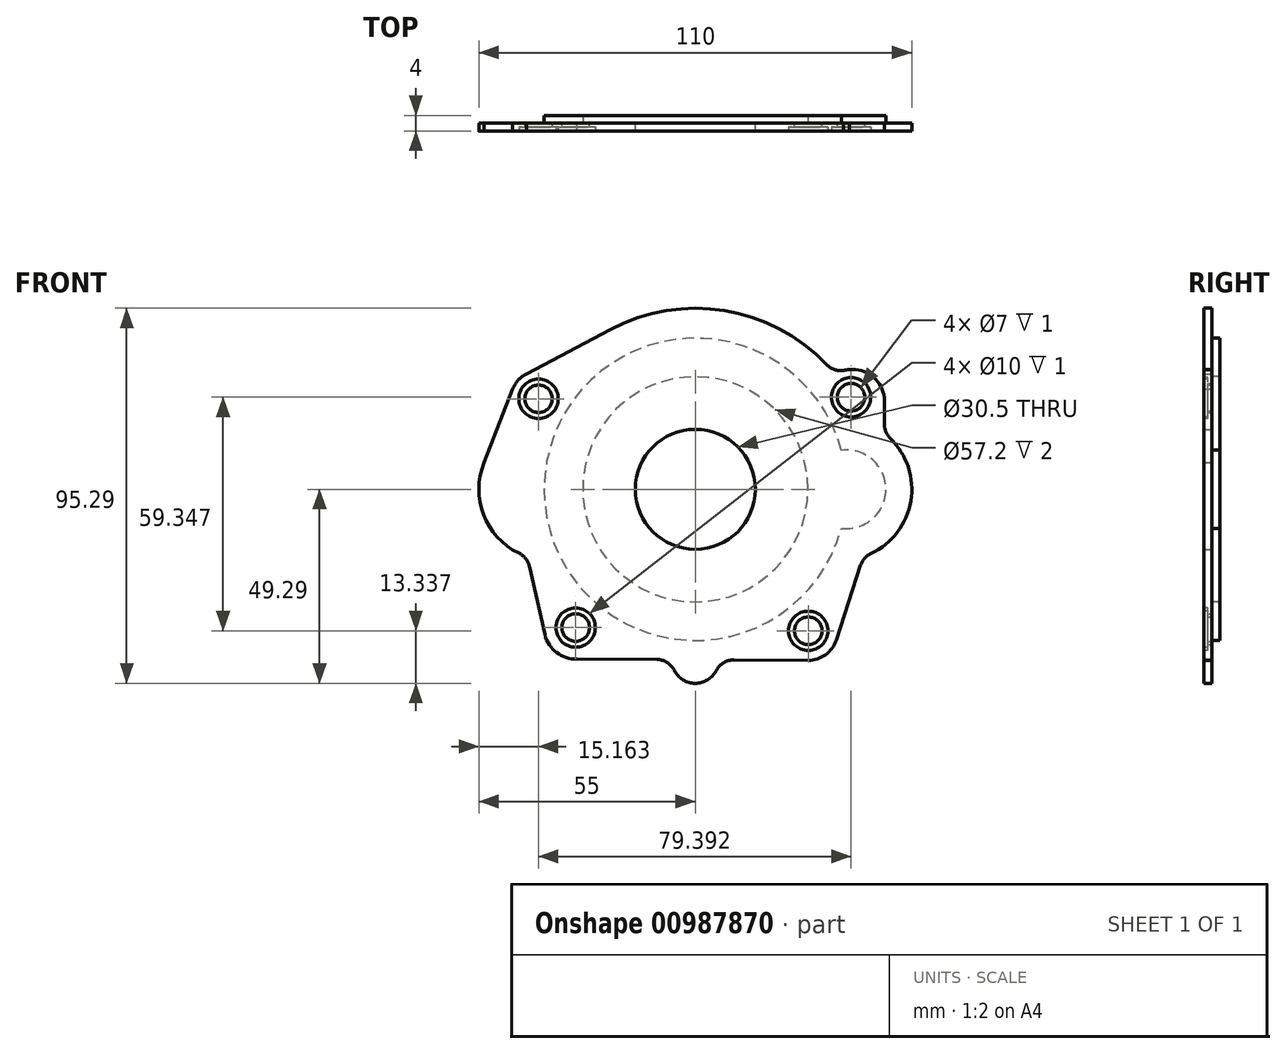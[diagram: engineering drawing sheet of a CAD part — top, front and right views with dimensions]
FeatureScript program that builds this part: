
annotation { "Feature Type Name" : "Feature", "Feature Type Description" : "" }
export const myFeature = defineFeature(function(context is Context, id is Id, definition is map)
    precondition{}
    {
        {
            var Q0;
            Q0=qCreatedBy(makeId("Front.planeOp"),FACE);
            var sketch = newSketch(context, id + "F0", { "sketchPlane" : qUnion([Q0])});
            skCircle(sketch, "E0", {"center": v(0, 0) * mm, "radius": 15.25 * mm});
            skCircle(sketch, "E1", {"center": v(-39.84, 23) * mm, "radius": 3.5 * mm});
            skCircle(sketch, "E2", {"center": v(-30.4, -35.12) * mm, "radius": 3.5 * mm});
            skCircle(sketch, "E3", {"center": v(28.7, -35.95) * mm, "radius": 3.5 * mm});
            skCircle(sketch, "E4", {"center": v(39.55, 23.4) * mm, "radius": 3.5 * mm});
            skArc(sketch, "E5", {"start": v(-42.72, -17.07) * mm, "mid": v(-39.64, -23.34) * mm, "end": v(-35.64, -29.08) * mm});
            skArc(sketch, "E6", {"start": v(-35.89, 28.78) * mm, "mid": v(-45.9, 26.5) * mm, "end": v(-42.87, 16.69) * mm});
            skArc(sketch, "E7", {"start": v(-35.64, -29.08) * mm, "mid": v(-35.64, -41.17) * mm, "end": v(-23.67, -39.44) * mm});
            skArc(sketch, "E8", {"start": v(22.47, -40.14) * mm, "mid": v(33.37, -41.81) * mm, "end": v(34.16, -30.81) * mm});
            skArc(sketch, "E9", {"start": v(42.7, 17.1) * mm, "mid": v(45.62, 26.98) * mm, "end": v(35.55, 29.2) * mm});
            skArc(sketch, "E10.trimOffspring", {"start": v(33.35, 31.68) * mm, "mid": v(7.38, 45.4) * mm, "end": v(-21.59, 40.62) * mm});
            skArc(sketch, "E11.trimOffspring", {"start": v(34.16, -30.81) * mm, "mid": v(39.05, -24.32) * mm, "end": v(42.72, -17.07) * mm});
            skArc(sketch, "E12", {"start": v(44.63, -16.3) * mm, "mid": v(54.75, -2.98) * mm, "end": v(49.53, 12.92) * mm});
            skArc(sketch, "E13.trimOffspring", {"start": v(42.72, 17.07) * mm, "mid": v(42.71, 17.08) * mm, "end": v(42.7, 17.1) * mm});
            skArc(sketch, "E14.MirrorCS", {"start": v(-44.84, -16.2) * mm, "mid": v(-53.8, -6.46) * mm, "end": v(-53.67, 6.78) * mm});
            skLineSegment(sketch, "E15", {"start": v(48.02, 16.5) * mm, "end": v(48.02, 22.98) * mm});
            skArc(sketch, "E16", {"start": v(47.9, 24.04) * mm, "mid": v(44.3, 29.2) * mm, "end": v(38.1, 30.26) * mm});
            skPoint(sketch, "E17.visualSharp", {"position": v(48.02, 23.39) * mm});
            skArc(sketch, "E17.filletArc", {"start": v(48.02, 22.98) * mm, "mid": v(47.99, 23.51) * mm, "end": v(47.9, 24.04) * mm});
            skPoint(sketch, "E18.newPointB", {"position": v(42.72, 17.07) * mm});
            skArc(sketch, "E18.filletArc", {"start": v(48.02, 16.5) * mm, "mid": v(48.41, 14.56) * mm, "end": v(49.53, 12.92) * mm});
            skPoint(sketch, "E19.visualSharp", {"position": v(35.55, 29.2) * mm});
            skArc(sketch, "E19.filletArc", {"start": v(33.35, 31.68) * mm, "mid": v(35.53, 30.34) * mm, "end": v(38.1, 30.26) * mm});
            skLineSegment(sketch, "E20", {"start": v(-46.39, 25.46) * mm, "end": v(-53.86, 6.3) * mm});
            skArc(sketch, "E21.trimOffspring", {"start": v(-43.24, 16.88) * mm, "mid": v(-42.98, 16.98) * mm, "end": v(-42.72, 17.07) * mm});
            skLineSegment(sketch, "E22", {"start": v(-42.86, 29.31) * mm, "end": v(-21.59, 40.62) * mm});
            skLineSegment(sketch, "E23", {"start": v(-30.86, -43.11) * mm, "end": v(-9.8, -43.23) * mm});
            skArc(sketch, "E24", {"start": v(-5.36, -45.98) * mm, "mid": v(-0.03, -49.29) * mm, "end": v(5.33, -46.05) * mm});
            skLineSegment(sketch, "E25.trimOffspring", {"start": v(9.8, -43.34) * mm, "end": v(28.65, -43.45) * mm});
            skPoint(sketch, "E26.visualSharp", {"position": v(-6, -43.25) * mm});
            skArc(sketch, "E26.filletArc", {"start": v(-5.36, -45.98) * mm, "mid": v(-7.2, -43.98) * mm, "end": v(-9.8, -43.23) * mm});
            skPoint(sketch, "E27.visualSharp", {"position": v(6, -43.32) * mm});
            skArc(sketch, "E27.filletArc", {"start": v(9.8, -43.34) * mm, "mid": v(7.18, -44.07) * mm, "end": v(5.33, -46.05) * mm});
            skLineSegment(sketch, "E28", {"start": v(-42.14, -19.6) * mm, "end": v(-38.2, -36.9) * mm});
            skPoint(sketch, "E29.visualSharp", {"position": v(-42.72, -17.07) * mm});
            skArc(sketch, "E29.filletArc", {"start": v(-42.14, -19.6) * mm, "mid": v(-43.1, -17.6) * mm, "end": v(-44.84, -16.2) * mm});
            skLineSegment(sketch, "E30", {"start": v(42, -19.29) * mm, "end": v(35.83, -38.27) * mm});
            skPoint(sketch, "E31.visualSharp", {"position": v(42.72, -17.07) * mm});
            skArc(sketch, "E31.filletArc", {"start": v(44.63, -16.3) * mm, "mid": v(43, -17.52) * mm, "end": v(42, -19.29) * mm});
            skSolve(sketch);
        }
        {
            var Q0;
            Q0 = qSketchRegion(id + "F0", true);
            extrude(context, id + "F1", {"entities" : qUnion([Q0]), "depth" : 2 * mm, "offsetDistance" : 25 * mm});
        }
        {
            var Q0;
            Q0=makeQuery(id+"F1.opExtrude","CAP_FACE",FACE,{"disambiguationData":[OSD([sQuery(id+"F0.wireOp",EDGE,"E0"),sQuery(id+"F0.wireOp",EDGE,"5DqQa9uN-ykfq-S9rf-LZpS-OIPvA6L4Fk4L")])],"isStart":true});
            var sketch = newSketch(context, id + "F2", { "sketchPlane" : qUnion([Q0])});
            skArc(sketch, "E32", {"start": v(-37.1, -9.91) * mm, "mid": v(38.4, 0) * mm, "end": v(-37.1, 9.91) * mm});
            skCircle(sketch, "E33", {"center": v(0, 0) * mm, "radius": 28.6 * mm});
            skArc(sketch, "E34", {"start": v(-37.1, 9.91) * mm, "mid": v(-48.4, 0) * mm, "end": v(-37.1, -9.91) * mm});
            skSolve(sketch);
        }
        {
            var Q0;
            Q0 = qSketchRegion(id + "F2", true);
            extrude(context, id + "F3", {"entities" : qUnion([Q0]), "operationType" : NewBodyOperationType.ADD, "depth" : 2 * mm, "offsetDistance" : 25 * mm});
        }
        {
            var Q0;
            Q0=makeQuery(id+"F1.opExtrude","CAP_FACE",FACE,{"disambiguationData":[OSD([sQuery(id+"F0.wireOp",EDGE,"E0"),sQuery(id+"F0.wireOp",EDGE,"5DqQa9uN-ykfq-S9rf-LZpS-OIPvA6L4Fk4L"),sQuery(id+"F0.wireOp",EDGE,"E1"),sQuery(id+"F0.wireOp",EDGE,"E2"),sQuery(id+"F0.wireOp",EDGE,"E3"),sQuery(id+"F0.wireOp",EDGE,"E4")])],"isStart":false});
            var sketch = newSketch(context, id + "F4", { "sketchPlane" : qUnion([Q0])});
            skCircle(sketch, "E35", {"center": v(-39.84, 23) * mm, "radius": 5 * mm});
            skCircle(sketch, "E36", {"center": v(39.55, 23.4) * mm, "radius": 5 * mm});
            skCircle(sketch, "E37", {"center": v(28.7, -35.95) * mm, "radius": 5 * mm});
            skCircle(sketch, "E38", {"center": v(-30.4, -35.12) * mm, "radius": 5 * mm});
            skSolve(sketch);
        }
        {
            var Q0;
            Q0=makeQuery(id+"F4.imprint","IMPRINT",FACE,{"disambiguationData":[TD([[makeQuery(id+"F4.imprint","IMPRINT",EDGE,{"derivedFrom":sQuery(id+"F4.wireOp",EDGE,"E35")}),1.0]])]});
            var Q1;
            Q1=makeQuery(id+"F4.imprint","IMPRINT",FACE,{"disambiguationData":[TD([[makeQuery(id+"F4.imprint","IMPRINT",EDGE,{"derivedFrom":sQuery(id+"F4.wireOp",EDGE,"E36")}),1.0]])]});
            var Q2;
            Q2=makeQuery(id+"F4.imprint","IMPRINT",FACE,{"disambiguationData":[TD([[makeQuery(id+"F4.imprint","IMPRINT",EDGE,{"derivedFrom":sQuery(id+"F4.wireOp",EDGE,"E37")}),1.0]])]});
            var Q3;
            Q3=makeQuery(id+"F4.imprint","IMPRINT",FACE,{"disambiguationData":[TD([[makeQuery(id+"F4.imprint","IMPRINT",EDGE,{"derivedFrom":sQuery(id+"F4.wireOp",EDGE,"E38")}),1.0]])]});
            extrude(context, id + "F5", {"entities" : qUnion([Q0, Q1, Q2, Q3]), "operationType" : NewBodyOperationType.REMOVE, "oppositeDirection" : true, "depth" : 1 * mm, "offsetDistance" : 25 * mm});
        }
    });
